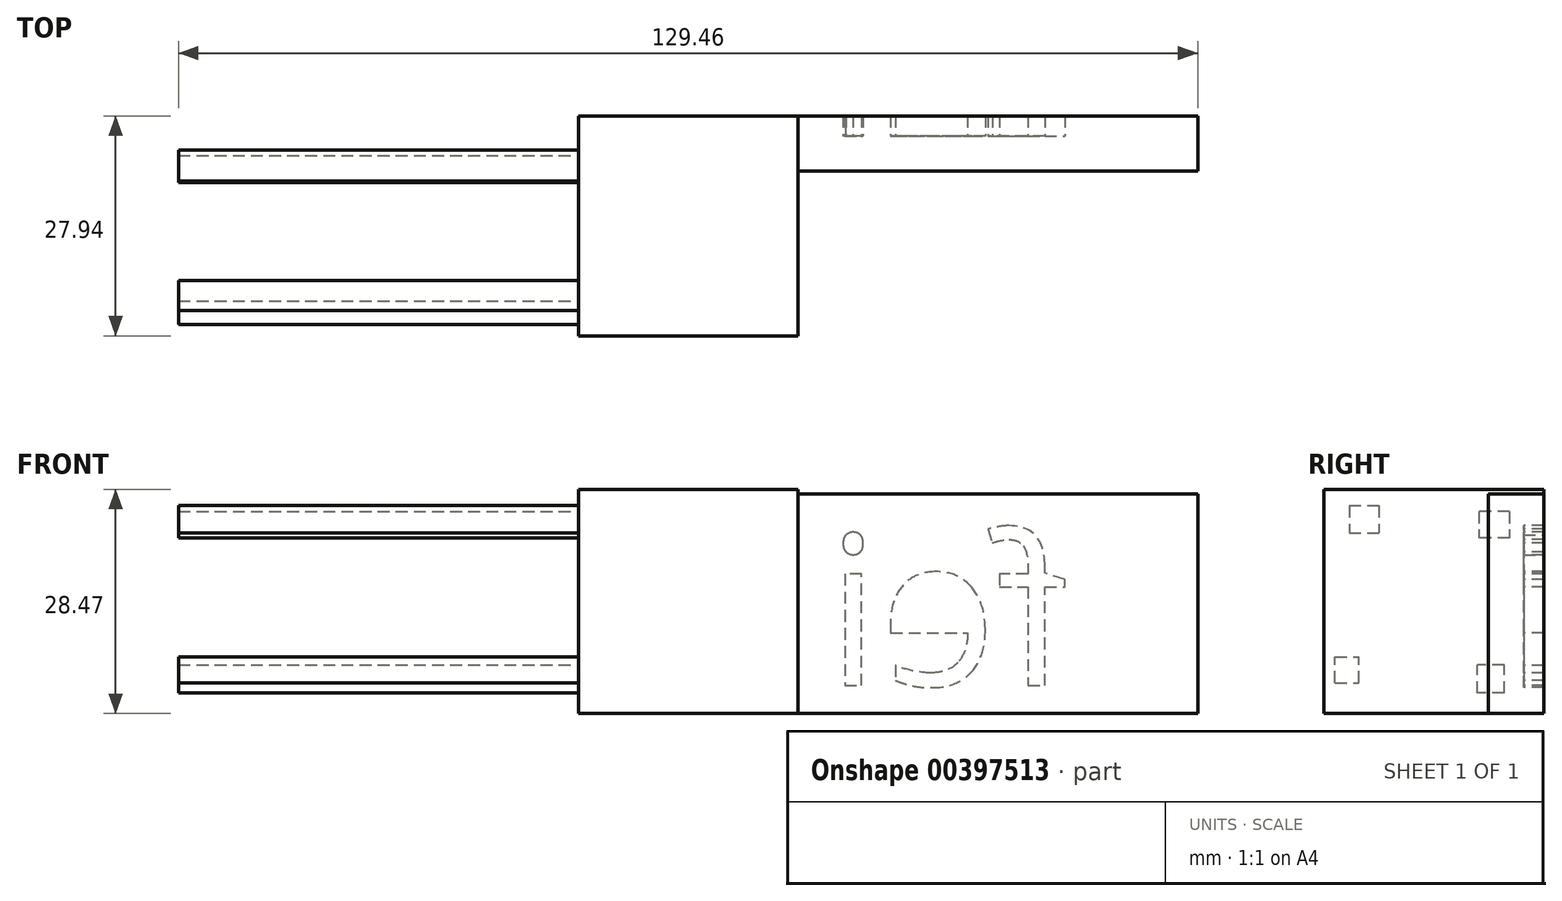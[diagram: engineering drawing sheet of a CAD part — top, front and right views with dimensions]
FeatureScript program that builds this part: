
annotation { "Feature Type Name" : "Feature", "Feature Type Description" : "" }
export const myFeature = defineFeature(function(context is Context, id is Id, definition is map)
    precondition{}
    {
        {
            var Q0;
            Q0=qCreatedBy(makeId("Front.planeOp"),FACE);
            var sketch = newSketch(context, id + "F0", { "sketchPlane" : qUnion([Q0])});
            skLineSegment(sketch, "E0.bottom", {"start": v(0, 0) * mm, "end": v(-27.86, 0) * mm});
            skLineSegment(sketch, "E0.top", {"start": v(0, -28.47) * mm, "end": v(-27.86, -28.47) * mm});
            skLineSegment(sketch, "E0.left", {"start": v(0, 0) * mm, "end": v(0, -28.47) * mm});
            skLineSegment(sketch, "E0.right", {"start": v(-27.86, 0) * mm, "end": v(-27.86, -28.47) * mm});
            skSolve(sketch);
        }
        {
            var Q0;
            Q0=makeQuery(id+"F0.imprint","IMPRINT",FACE,{"disambiguationData":[TD([[makeQuery(id+"F0.imprint","IMPRINT",EDGE,{"derivedFrom":sQuery(id+"F0.wireOp",EDGE,"E0.bottom")}),1.0]])]});
            extrude(context, id + "F1", {"entities" : qUnion([Q0]), "depth" : 25.4 * mm});
        }
        {
            var Q0;
            Q0=makeQuery(id+"F1.opExtrude","SWEPT_FACE",FACE,{"disambiguationData":[OSD([sQuery(id+"F0.wireOp",EDGE,"E0.right")])]});
            var sketch = newSketch(context, id + "F2", { "sketchPlane" : qUnion([Q0])});
            skLineSegment(sketch, "E1.bottom", {"start": v(1.8, -2.8) * mm, "end": v(5.71, -2.8) * mm});
            skLineSegment(sketch, "E1.top", {"start": v(1.8, -6.18) * mm, "end": v(5.71, -6.18) * mm});
            skLineSegment(sketch, "E1.left", {"start": v(1.8, -2.8) * mm, "end": v(1.8, -6.18) * mm});
            skLineSegment(sketch, "E1.right", {"start": v(5.71, -2.8) * mm, "end": v(5.71, -6.18) * mm});
            skSolve(sketch);
        }
        {
            var Q0;
            Q0=makeQuery(id+"F2.imprint","IMPRINT",FACE,{"disambiguationData":[TD([[makeQuery(id+"F2.imprint","IMPRINT",EDGE,{"derivedFrom":sQuery(id+"F2.wireOp",EDGE,"E1.bottom")}),-1.0]])]});
            extrude(context, id + "F3", {"entities" : qUnion([Q0]), "operationType" : NewBodyOperationType.ADD, "depth" : 50.8 * mm});
        }
        {
            var Q0;
            Q0=makeQuery(id+"F1.opExtrude","SWEPT_FACE",FACE,{"disambiguationData":[OSD([sQuery(id+"F0.wireOp",EDGE,"E0.right")])]});
            var sketch = newSketch(context, id + "F4", { "sketchPlane" : qUnion([Q0])});
            skLineSegment(sketch, "E2.bottom", {"start": v(22.17, -2.07) * mm, "end": v(18.36, -2.07) * mm});
            skLineSegment(sketch, "E2.top", {"start": v(22.17, -5.52) * mm, "end": v(18.36, -5.52) * mm});
            skLineSegment(sketch, "E2.left", {"start": v(22.17, -2.07) * mm, "end": v(22.17, -5.52) * mm});
            skLineSegment(sketch, "E2.right", {"start": v(18.36, -2.07) * mm, "end": v(18.36, -5.52) * mm});
            skSolve(sketch);
        }
        {
            var Q0;
            Q0=makeQuery(id+"F4.imprint","IMPRINT",FACE,{"disambiguationData":[TD([[makeQuery(id+"F4.imprint","IMPRINT",EDGE,{"derivedFrom":sQuery(id+"F4.wireOp",EDGE,"E2.bottom")}),1.0]])]});
            extrude(context, id + "F5", {"entities" : qUnion([Q0]), "operationType" : NewBodyOperationType.ADD, "depth" : 50.8 * mm});
        }
        {
            var Q0;
            Q0=makeQuery(id+"F1.opExtrude","SWEPT_FACE",FACE,{"disambiguationData":[OSD([sQuery(id+"F0.wireOp",EDGE,"E0.right")])]});
            var sketch = newSketch(context, id + "F6", { "sketchPlane" : qUnion([Q0])});
            skLineSegment(sketch, "E3.bottom", {"start": v(2.47, -25.88) * mm, "end": v(5.9, -25.88) * mm});
            skLineSegment(sketch, "E3.top", {"start": v(2.47, -22.27) * mm, "end": v(5.9, -22.27) * mm});
            skLineSegment(sketch, "E3.left", {"start": v(2.47, -25.88) * mm, "end": v(2.47, -22.27) * mm});
            skLineSegment(sketch, "E3.right", {"start": v(5.9, -25.88) * mm, "end": v(5.9, -22.27) * mm});
            skSolve(sketch);
        }
        {
            var Q0;
            Q0=makeQuery(id+"F6.imprint","IMPRINT",FACE,{"disambiguationData":[TD([[makeQuery(id+"F6.imprint","IMPRINT",EDGE,{"derivedFrom":sQuery(id+"F6.wireOp",EDGE,"E3.bottom")}),1.0]])]});
            extrude(context, id + "F7", {"entities" : qUnion([Q0]), "operationType" : NewBodyOperationType.ADD, "depth" : 50.8 * mm});
        }
        {
            var Q0;
            Q0=makeQuery(id+"F1.opExtrude","SWEPT_FACE",FACE,{"disambiguationData":[OSD([sQuery(id+"F0.wireOp",EDGE,"E0.left")])]});
            var sketch = newSketch(context, id + "F8", { "sketchPlane" : qUnion([Q0])});
            skLineSegment(sketch, "E4.bottom", {"start": v(0, -0.57) * mm, "end": v(-4.46, -0.57) * mm});
            skLineSegment(sketch, "E4.top", {"start": v(0, -28.47) * mm, "end": v(-4.46, -28.47) * mm});
            skLineSegment(sketch, "E4.left", {"start": v(0, -0.57) * mm, "end": v(0, -28.47) * mm});
            skLineSegment(sketch, "E4.right", {"start": v(-4.46, -0.57) * mm, "end": v(-4.46, -28.47) * mm});
            skSolve(sketch);
        }
        {
            var Q0;
            Q0=makeQuery(id+"F1.opExtrude","SWEPT_FACE",FACE,{"disambiguationData":[OSD([sQuery(id+"F0.wireOp",EDGE,"E0.right")])]});
            var sketch = newSketch(context, id + "F9", { "sketchPlane" : qUnion([Q0])});
            skLineSegment(sketch, "E5.bottom", {"start": v(23.95, -24.57) * mm, "end": v(20.94, -24.57) * mm});
            skLineSegment(sketch, "E5.top", {"start": v(23.95, -21.28) * mm, "end": v(20.94, -21.28) * mm});
            skLineSegment(sketch, "E5.left", {"start": v(23.95, -24.57) * mm, "end": v(23.95, -21.28) * mm});
            skLineSegment(sketch, "E5.right", {"start": v(20.94, -24.57) * mm, "end": v(20.94, -21.28) * mm});
            skSolve(sketch);
        }
        {
            var Q0;
            Q0=makeQuery(id+"F9.imprint","IMPRINT",FACE,{"disambiguationData":[TD([[makeQuery(id+"F9.imprint","IMPRINT",EDGE,{"derivedFrom":sQuery(id+"F9.wireOp",EDGE,"E5.bottom")}),-1.0]])]});
            extrude(context, id + "F10", {"entities" : qUnion([Q0]), "operationType" : NewBodyOperationType.ADD, "depth" : 50.8 * mm});
        }
        {
            var Q0;
            Q0=makeQuery(id+"F8.imprint","IMPRINT",FACE,{"disambiguationData":[TD([[makeQuery(id+"F8.imprint","IMPRINT",EDGE,{"derivedFrom":sQuery(id+"F8.wireOp",EDGE,"E4.bottom")}),1.0]])]});
            extrude(context, id + "F11", {"entities" : qUnion([Q0]), "operationType" : NewBodyOperationType.ADD, "depth" : 50.8 * mm});
        }
        {
            var Q0;
            Q0=makeQuery(id+"F11.boolean.opBoolean","MERGE",FACE,{"derivedFrom":[makeQuery(id+"F1.opExtrude","CAP_FACE",FACE,{"disambiguationData":[OSD([sQuery(id+"F0.wireOp",EDGE,"E0.bottom"),sQuery(id+"F0.wireOp",EDGE,"E0.top"),sQuery(id+"F0.wireOp",EDGE,"E0.left"),sQuery(id+"F0.wireOp",EDGE,"E0.right")])],"isStart":true}),makeQuery(id+"F11.opExtrude","SWEPT_FACE",FACE,{"disambiguationData":[OSD([sQuery(id+"F8.wireOp",EDGE,"E4.left")])]})]});
            var sketch = newSketch(context, id + "F12", { "sketchPlane" : qUnion([Q0])});
            skText(sketch, "E6", { "text": "fei", "fontName": "OpenSans-Regular.ttf"});
            const initialGuessF12  = {"E6": [-0.0343, -0.02492, 1, 0, 0.01912]};
            skSetInitialGuess(sketch, initialGuessF12);
            skSolve(sketch);
        }
        {
            var Q0;
            Q0=makeQuery(id+"F12.imprint","IMPRINT",FACE,{"disambiguationData":[TD([[makeQuery(id+"F12.imprint","IMPRINT",EDGE,{"derivedFrom":sQuery(id+"F12.wireOp",EDGE,"E6.sketch_text.stroke-0")}),1.0]])]});
            extrude(context, id + "F13", {"entities" : qUnion([Q0]), "operationType" : NewBodyOperationType.ADD, "depth" : 2.54 * mm});
        }
    });
